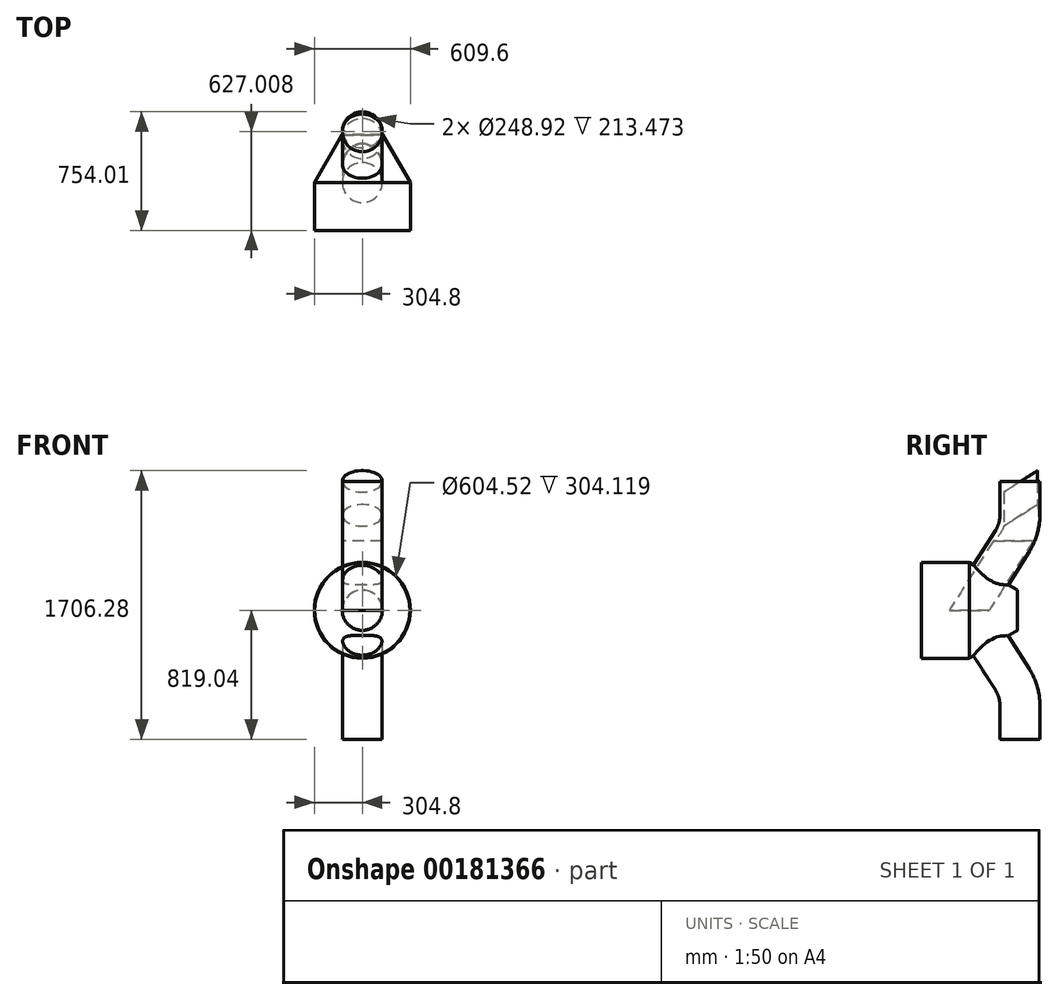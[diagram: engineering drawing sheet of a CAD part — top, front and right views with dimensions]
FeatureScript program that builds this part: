
annotation { "Feature Type Name" : "Feature", "Feature Type Description" : "" }
export const myFeature = defineFeature(function(context is Context, id is Id, definition is map)
    precondition{}
    {
        {
            var Q0;
            Q0=qCreatedBy(makeId("Front.planeOp"),FACE);
            var sketch = newSketch(context, id + "F0", { "sketchPlane" : qUnion([Q0])});
            skCircle(sketch, "E0", {"center": v(0, 0) * mm, "radius": 304.8 * mm});
            skSolve(sketch);
        }
        {
            var Q0;
            Q0=makeQuery(id+"F0.imprint","IMPRINT",FACE,{"disambiguationData":[TD([[makeQuery(id+"F0.imprint","IMPRINT",EDGE,{"derivedFrom":sQuery(id+"F0.wireOp",EDGE,"E0")}),1.0]])]});
            extrude(context, id + "F1", {"entities" : qUnion([Q0]), "depth" : 304.8 * mm});
        }
        {
            var Q0;
            Q0 = qSketchRegion(id + "F0", true);
            extrude(context, id + "F2", {"entities" : qUnion([Q0]), "operationType" : NewBodyOperationType.ADD, "oppositeDirection" : true, "depth" : 304.8 * mm, "hasDraft" : true, "draftAngle" : 30 * degree, "draftPullDirection" : true});
        }
        {
            var Q0;
            Q0=qCreatedBy(makeId("Right.planeOp"),FACE);
            var sketch = newSketch(context, id + "F3", { "sketchPlane" : qUnion([Q0])});
            skLineSegment(sketch, "E1", {"start": v(0, 0) * mm, "end": v(279.69, 439.34) * mm});
            skLineSegment(sketch, "E2", {"start": v(327.37, 603.03) * mm, "end": v(327.37, 819.04) * mm});
            skPoint(sketch, "E3.visualSharp", {"position": v(327.37, 514.24) * mm});
            skArc(sketch, "E3.filletArc", {"start": v(279.69, 439.34) * mm, "mid": v(315.2, 517.78) * mm, "end": v(327.37, 603.03) * mm});
            skSolve(sketch);
        }
        {
            var Q0;
            Q0=qCreatedBy(makeId("Top.planeOp"),FACE);
            var sketch = newSketch(context, id + "F4", { "sketchPlane" : qUnion([Q0])});
            skCircle(sketch, "E4", {"center": v(0, 0) * mm, "radius": 127 * mm});
            skSolve(sketch);
        }
        {
            var Q0;
            Q0=qCreatedBy(makeId("Top.planeOp"),FACE);
            cPlane(context, id + "F5", {"entities" : qUnion([Q0]), "cplaneType" : CPlaneType.OFFSET, "offset" : 819.04 * mm, "width" : 152.4 * mm, "height" : 152.4 * mm});
        }
        {
            var Q0;
            Q0=qCreatedBy(id+"F5.planeOp",FACE);
            var sketch = newSketch(context, id + "F6", { "sketchPlane" : qUnion([Q0])});
            skCircle(sketch, "E5", {"center": v(0, 322.2) * mm, "radius": 127 * mm});
            skSolve(sketch);
        }
        {
            var Q0;
            Q0=makeQuery(id+"F6.imprint","IMPRINT",FACE,{"disambiguationData":[TD([[makeQuery(id+"F6.imprint","IMPRINT",EDGE,{"derivedFrom":sQuery(id+"F6.wireOp",EDGE,"E5")}),1.0]])]});
            var Q1;
            Q1=sQuery(id+"F3.wireOp",EDGE,"E2");
            var Q2;
            Q2=sQuery(id+"F3.wireOp",EDGE,"E3.filletArc");
            var Q3;
            Q3=sQuery(id+"F3.wireOp",EDGE,"E1");
            sweep(context, id + "F7", {"operationType" : NewBodyOperationType.ADD, "profiles" : qUnion([Q0]), "path" : qUnion([Q1, Q2, Q3])});
        }
        {
            var Q0;
            Q0=makeQuery(id+"F1.opExtrude","SWEPT_BODY",BODY,{"disambiguationData":[OSD([sQuery(id+"F0.wireOp",EDGE,"E0")])]});
            var Q1;
            Q1=qCreatedBy(makeId("Top.planeOp"),FACE);
            mirror(context, id + "F8", {"operationType" : NewBodyOperationType.ADD, "entities" : qUnion([Q0]), "mirrorPlane" : qUnion([Q1])});
        }
        {
            var Q0;
            Q0=makeQuery(id+"F1.opExtrude","CAP_FACE",FACE,{"disambiguationData":[OSD([sQuery(id+"F0.wireOp",EDGE,"E0")])],"isStart":false});
            var Q1;
            Q1=makeQuery(id+"F7.opSweep","CAP_FACE",FACE,{"disambiguationData":[OSD([sQuery(id+"F3.wireOp",VERTEX,"E2.end"),sQuery(id+"F6.wireOp",EDGE,"E5")])],"isStart":true});
            var Q2;
            Q2=makeQuery(id+"F8.opPattern","COPY",FACE,{"derivedFrom":makeQuery(id+"F7.opSweep","CAP_FACE",FACE,{"disambiguationData":[OSD([sQuery(id+"F3.wireOp",VERTEX,"E2.end"),sQuery(id+"F6.wireOp",EDGE,"E5")])],"isStart":true}),"instanceName":"1"});
            shell(context, id + "F9", {"entities" : qUnion([Q0, Q1, Q2]), "thickness" : 2.54 * mm});
        }
        {
            var Q0;
            Q0=makeQuery(id+"F4.imprint","IMPRINT",FACE,{"disambiguationData":[TD([[makeQuery(id+"F4.imprint","IMPRINT",EDGE,{"derivedFrom":sQuery(id+"F4.wireOp",EDGE,"E4")}),1.0]])]});
            var Q1;
            Q1=sQuery(id+"F3.wireOp",EDGE,"E1");
            var Q2;
            Q2=sQuery(id+"F3.wireOp",EDGE,"E3.filletArc");
            var Q3;
            Q3=sQuery(id+"F3.wireOp",EDGE,"E2");
            sweep(context, id + "F10", {"profiles" : qUnion([Q0]), "path" : qUnion([Q1, Q2, Q3])});
        }
    });
